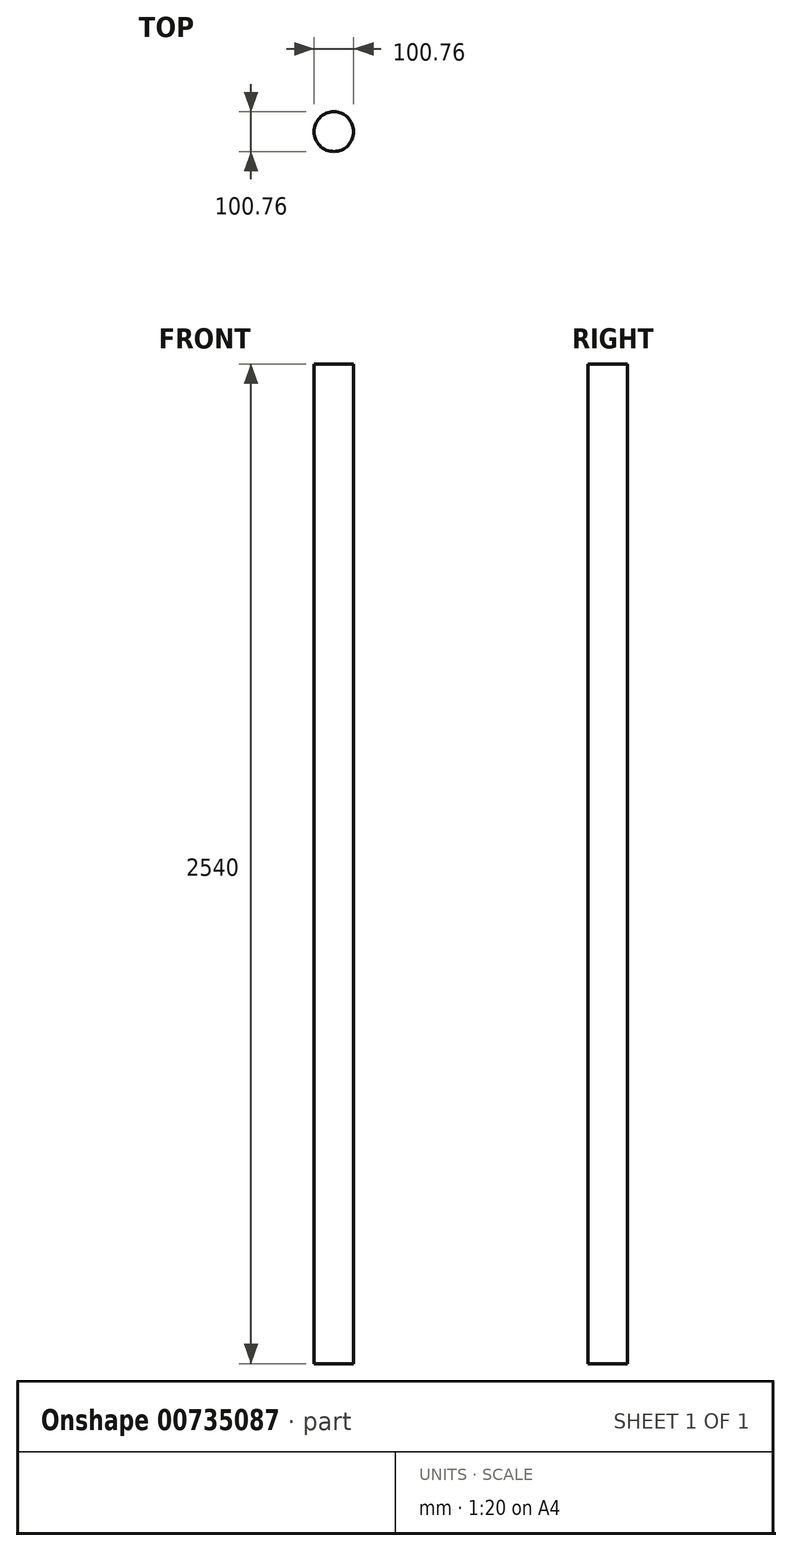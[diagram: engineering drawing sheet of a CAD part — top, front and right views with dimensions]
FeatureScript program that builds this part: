
annotation { "Feature Type Name" : "Feature", "Feature Type Description" : "" }
export const myFeature = defineFeature(function(context is Context, id is Id, definition is map)
    precondition{}
    {
        {
            var Q0;
            Q0=qCreatedBy(makeId("Top.planeOp"),FACE);
            var sketch = newSketch(context, id + "F0", { "sketchPlane" : qUnion([Q0])});
            skCircle(sketch, "E0", {"center": v(0, 0) * mm, "radius": 50.38 * mm});
            skSolve(sketch);
        }
        {
            var Q0;
            Q0 = qSketchRegion(id + "F0", true);
            extrude(context, id + "F1", {"entities" : qUnion([Q0]), "depth" : 2540 * mm, "offsetDistance" : 25.4 * mm});
        }
    });
